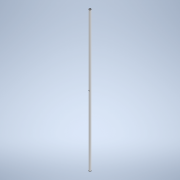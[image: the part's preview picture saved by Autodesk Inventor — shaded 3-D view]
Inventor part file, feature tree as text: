
AUTODESK INVENTOR PART (.ipt)
format: ipt  version: 2021 (Build 250183000, 183)  size: 113,152 bytes
history: native  units: mm
features: sketch x4, extrude x2, hole x2, thread x1
ambient origin geometry x8: Origin, YZ Plane, XZ Plane, XY Plane, X Axis, Y Axis, Z Axis, Center Point
bodies: Solid1 (feature_tree)
feature tree (9):
  extrude  "Extrusion1"  Depth=800.0mm TaperAngle=0.0deg
  hole  "Hole1"  [1 undecoded]
  hole  "Hole2"  [1 undecoded]
  extrude  "Extrusion3"  [1 undecoded]
  thread  "Thread2"  [1 undecoded]
  sketch  "Sketch1"  dims[d0=12.0mm d1=800.0mm d2=0.0mm]
  sketch  "Sketch2"  dims[d3=8.0mm d4=6.0mm d5=4.0mm d6=2.0mm d7=90.0deg d8=33.0mm d9=20.594885mm]
  sketch  "Sketch3"  dims[d10=8.0mm d11=6.0mm d12=4.0mm d13=2.0mm d14=90.0deg d15=33.0mm d16=20.594885mm d22=4.0mm]
  sketch  "Sketch5"  dims[d23=0.0mm d24=0.0mm d25=12.0mm d26=0.0mm]
note: 4 required parameter values undecoded (feature->parameter linkage not recoverable at this tier; creation-order binding heuristic only, values carry confidence <= 0.55)
